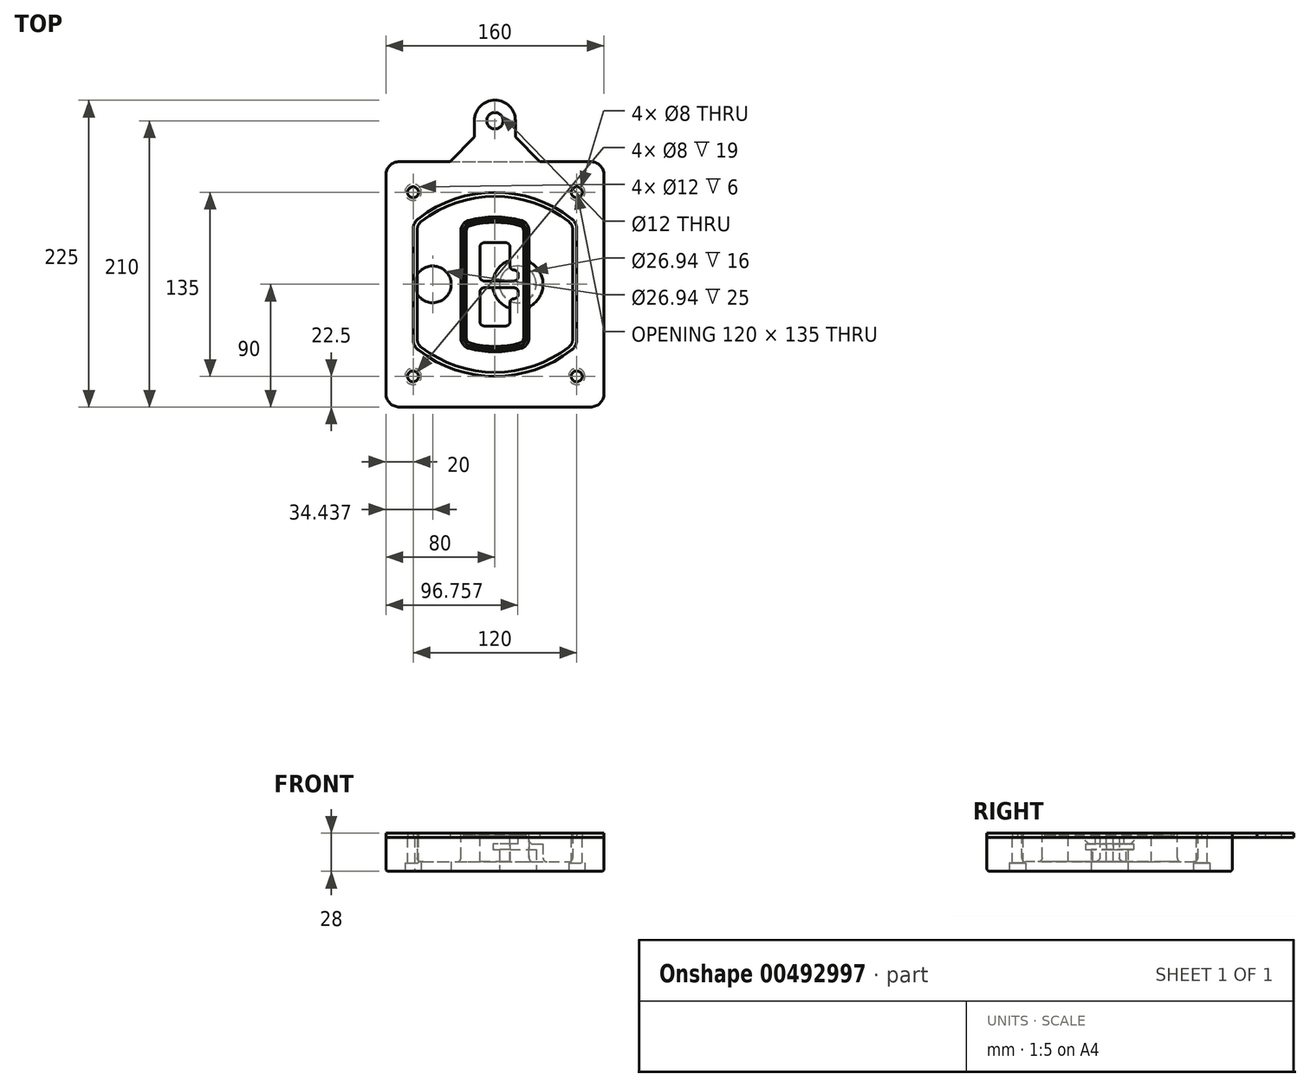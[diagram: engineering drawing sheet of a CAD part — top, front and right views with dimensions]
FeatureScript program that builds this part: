
annotation { "Feature Type Name" : "Feature", "Feature Type Description" : "" }
export const myFeature = defineFeature(function(context is Context, id is Id, definition is map)
    precondition{}
    {
        {
            var Q0;
            Q0=qCreatedBy(makeId("Top.planeOp"),FACE);
            var sketch = newSketch(context, id + "F0", { "sketchPlane" : qUnion([Q0])});
            skPoint(sketch, "E0.rect.middle", {"position": v(0, 0) * mm});
            skLineSegment(sketch, "E1.bottom", {"start": v(-70, -90) * mm, "end": v(70, -90) * mm});
            skLineSegment(sketch, "E1.top", {"start": v(-70, 90) * mm, "end": v(70, 90) * mm});
            skLineSegment(sketch, "E1.left", {"start": v(-80, -80) * mm, "end": v(-80, 80) * mm});
            skLineSegment(sketch, "E1.right", {"start": v(80, -80) * mm, "end": v(80, 80) * mm});
            skLineSegment(sketch, "E2", {"start": v(-80, 90) * mm, "end": v(80, -90) * mm, "construction": true});
            skLineSegment(sketch, "E3", {"start": v(80, 90) * mm, "end": v(-80, -90) * mm, "construction": true});
            skCircle(sketch, "E4", {"center": v(-60, 67.5) * mm, "radius": 4 * mm});
            skCircle(sketch, "E5", {"center": v(60, 67.5) * mm, "radius": 4 * mm});
            skCircle(sketch, "E6", {"center": v(60, -67.5) * mm, "radius": 4 * mm});
            skCircle(sketch, "E7", {"center": v(-60, -67.5) * mm, "radius": 4 * mm});
            skLineSegment(sketch, "E8", {"start": v(-60, 67.5) * mm, "end": v(60, 67.5) * mm, "construction": true});
            skLineSegment(sketch, "E9", {"start": v(60, 67.5) * mm, "end": v(60, -67.5) * mm, "construction": true});
            skLineSegment(sketch, "E10", {"start": v(60, -67.5) * mm, "end": v(-60, -67.5) * mm, "construction": true});
            skLineSegment(sketch, "E11", {"start": v(-60, -67.5) * mm, "end": v(-60, 67.5) * mm, "construction": true});
            skLineSegment(sketch, "E12", {"start": v(-60, 40.3) * mm, "end": v(-60, -40.3) * mm});
            skLineSegment(sketch, "E13", {"start": v(60, 40.3) * mm, "end": v(60, -40.3) * mm});
            skArc(sketch, "E14", {"start": v(56.15, 48.18) * mm, "mid": v(0, 67.5) * mm, "end": v(-56.15, 48.18) * mm});
            skArc(sketch, "E15", {"start": v(-56.15, -48.18) * mm, "mid": v(0, -67.5) * mm, "end": v(56.15, -48.18) * mm});
            skLineSegment(sketch, "E16", {"start": v(-60, 0) * mm, "end": v(60, 0) * mm, "construction": true});
            skPoint(sketch, "E17.visualSharp", {"position": v(-60, -45) * mm});
            skArc(sketch, "E17.filletArc", {"start": v(-60, -40.3) * mm, "mid": v(-58.99, -44.68) * mm, "end": v(-56.15, -48.18) * mm});
            skPoint(sketch, "E18.visualSharp", {"position": v(-60, 45) * mm});
            skArc(sketch, "E18.filletArc", {"start": v(-56.15, 48.18) * mm, "mid": v(-58.99, 44.68) * mm, "end": v(-60, 40.3) * mm});
            skPoint(sketch, "E19.visualSharp", {"position": v(60, 45) * mm});
            skArc(sketch, "E19.filletArc", {"start": v(60, 40.3) * mm, "mid": v(58.99, 44.68) * mm, "end": v(56.15, 48.18) * mm});
            skPoint(sketch, "E20.visualSharp", {"position": v(60, -45) * mm});
            skArc(sketch, "E20.filletArc", {"start": v(56.15, -48.18) * mm, "mid": v(58.99, -44.68) * mm, "end": v(60, -40.3) * mm});
            skPoint(sketch, "E21.visualSharp", {"position": v(-80, 90) * mm});
            skArc(sketch, "E21.filletArc", {"start": v(-70, 90) * mm, "mid": v(-77.07, 87.07) * mm, "end": v(-80, 80) * mm});
            skPoint(sketch, "E22.visualSharp", {"position": v(80, 90) * mm});
            skArc(sketch, "E22.filletArc", {"start": v(80, 80) * mm, "mid": v(77.07, 87.07) * mm, "end": v(70, 90) * mm});
            skPoint(sketch, "E23.visualSharp", {"position": v(80, -90) * mm});
            skArc(sketch, "E23.filletArc", {"start": v(70, -90) * mm, "mid": v(77.07, -87.07) * mm, "end": v(80, -80) * mm});
            skPoint(sketch, "E24.visualSharp", {"position": v(-80, -90) * mm});
            skArc(sketch, "E24.filletArc", {"start": v(-80, -80) * mm, "mid": v(-77.07, -87.07) * mm, "end": v(-70, -90) * mm});
            skArc(sketch, "E25.0", {"start": v(57, 40.3) * mm, "mid": v(56.3, 43.36) * mm, "end": v(54.3, 45.81) * mm});
            skLineSegment(sketch, "E25.1", {"start": v(57, 40.3) * mm, "end": v(57, -40.3) * mm});
            skArc(sketch, "E25.2", {"start": v(54.3, -45.81) * mm, "mid": v(56.3, -43.36) * mm, "end": v(57, -40.3) * mm});
            skArc(sketch, "E25.3", {"start": v(-54.3, -45.81) * mm, "mid": v(0, -64.5) * mm, "end": v(54.3, -45.81) * mm});
            skArc(sketch, "E25.4", {"start": v(-57, -40.3) * mm, "mid": v(-56.3, -43.36) * mm, "end": v(-54.3, -45.81) * mm});
            skArc(sketch, "E25.5", {"start": v(54.3, 45.81) * mm, "mid": v(0, 64.5) * mm, "end": v(-54.3, 45.81) * mm});
            skLineSegment(sketch, "E25.6", {"start": v(-57, 40.3) * mm, "end": v(-57, -40.3) * mm});
            skArc(sketch, "E25.7", {"start": v(-54.3, 45.81) * mm, "mid": v(-56.3, 43.36) * mm, "end": v(-57, 40.3) * mm});
            skArc(sketch, "E26.0", {"start": v(-58.62, 51.33) * mm, "mid": v(-62.58, 46.43) * mm, "end": v(-64, 40.3) * mm});
            skArc(sketch, "E26.1", {"start": v(58.62, 51.33) * mm, "mid": v(0, 71.5) * mm, "end": v(-58.62, 51.33) * mm});
            skArc(sketch, "E26.2", {"start": v(64, 40.3) * mm, "mid": v(62.58, 46.43) * mm, "end": v(58.62, 51.33) * mm});
            skLineSegment(sketch, "E26.3", {"start": v(64, 40.3) * mm, "end": v(64, -40.3) * mm});
            skArc(sketch, "E26.4", {"start": v(58.62, -51.33) * mm, "mid": v(62.58, -46.43) * mm, "end": v(64, -40.3) * mm});
            skLineSegment(sketch, "E26.5", {"start": v(-64, 40.3) * mm, "end": v(-64, -40.3) * mm});
            skArc(sketch, "E26.6", {"start": v(-58.62, -51.33) * mm, "mid": v(0, -71.5) * mm, "end": v(58.62, -51.33) * mm});
            skArc(sketch, "E26.7", {"start": v(-64, -40.3) * mm, "mid": v(-62.58, -46.43) * mm, "end": v(-58.62, -51.33) * mm});
            skSolve(sketch);
        }
        {
            var Q0;
            Q0=makeQuery(id+"F0.imprint","IMPRINT",FACE,{"disambiguationData":[TD([[makeQuery(id+"F0.imprint","IMPRINT",EDGE,{"derivedFrom":sQuery(id+"F0.wireOp",EDGE,"E1.bottom")}),1.0]])]});
            var Q1;
            Q1=makeQuery(id+"F0.imprint","IMPRINT",FACE,{"disambiguationData":[TD([[makeQuery(id+"F0.imprint","IMPRINT",EDGE,{"derivedFrom":sQuery(id+"F0.wireOp",EDGE,"E12")}),1.0]])]});
            var Q2;
            Q2=makeQuery(id+"F0.imprint","IMPRINT",FACE,{"disambiguationData":[TD([[makeQuery(id+"F0.imprint","IMPRINT",EDGE,{"derivedFrom":sQuery(id+"F0.wireOp",EDGE,"E25.0")}),1.0]])]});
            var Q3;
            Q3=makeQuery(id+"F0.imprint","IMPRINT",FACE,{"disambiguationData":[TD([[makeQuery(id+"F0.imprint","IMPRINT",EDGE,{"derivedFrom":sQuery(id+"F0.wireOp",EDGE,"E12")}),-1.0]])]});
            extrude(context, id + "F1", {"entities" : qUnion([Q0, Q1, Q2, Q3]), "oppositeDirection" : true, "depth" : 25 * mm});
        }
        {
            var Q0;
            Q0=makeQuery(id+"F0.imprint","IMPRINT",FACE,{"disambiguationData":[TD([[makeQuery(id+"F0.imprint","IMPRINT",EDGE,{"derivedFrom":sQuery(id+"F0.wireOp",EDGE,"E12")}),1.0]])]});
            extrude(context, id + "F2", {"entities" : qUnion([Q0]), "operationType" : NewBodyOperationType.ADD, "depth" : 3 * mm});
        }
        {
            var Q0;
            Q0=makeQuery(id+"F0.imprint","IMPRINT",FACE,{"disambiguationData":[TD([[makeQuery(id+"F0.imprint","IMPRINT",EDGE,{"derivedFrom":sQuery(id+"F0.wireOp",EDGE,"E25.0")}),1.0]])]});
            extrude(context, id + "F3", {"entities" : qUnion([Q0]), "operationType" : NewBodyOperationType.REMOVE, "oppositeDirection" : true, "depth" : 18 * mm});
        }
        {
            var Q0;
            Q0=makeQuery(id+"F2.opExtrude","CAP_FACE",FACE,{"disambiguationData":[OSD([sQuery(id+"F0.wireOp",EDGE,"E12"),sQuery(id+"F0.wireOp",EDGE,"E13"),sQuery(id+"F0.wireOp",EDGE,"E14"),sQuery(id+"F0.wireOp",EDGE,"E15"),sQuery(id+"F0.wireOp",EDGE,"E17.filletArc"),sQuery(id+"F0.wireOp",EDGE,"E18.filletArc"),sQuery(id+"F0.wireOp",EDGE,"E19.filletArc"),sQuery(id+"F0.wireOp",EDGE,"E20.filletArc"),sQuery(id+"F0.wireOp",EDGE,"E25.0"),sQuery(id+"F0.wireOp",EDGE,"E25.1"),sQuery(id+"F0.wireOp",EDGE,"E25.2"),sQuery(id+"F0.wireOp",EDGE,"E25.3"),sQuery(id+"F0.wireOp",EDGE,"E25.4"),sQuery(id+"F0.wireOp",EDGE,"E25.5"),sQuery(id+"F0.wireOp",EDGE,"E25.6"),sQuery(id+"F0.wireOp",EDGE,"E25.7")])],"isStart":false});
            var sketch = newSketch(context, id + "F4", { "sketchPlane" : qUnion([Q0])});
            skArc(sketch, "E27.0", {"start": v(-19.08, -46.97) * mm, "mid": v(0, -49.5) * mm, "end": v(19.08, -46.97) * mm});
            skArc(sketch, "E28.0", {"start": v(19.08, 46.97) * mm, "mid": v(0, 49.5) * mm, "end": v(-19.08, 46.97) * mm});
            skLineSegment(sketch, "E29", {"start": v(-25, 39.25) * mm, "end": v(-25, -39.25) * mm});
            skLineSegment(sketch, "E30", {"start": v(25, 39.25) * mm, "end": v(25, -39.25) * mm});
            skLineSegment(sketch, "E31", {"start": v(-25, 45.1) * mm, "end": v(25, 45.1) * mm, "construction": true});
            skLineSegment(sketch, "E32", {"start": v(-25, -45.1) * mm, "end": v(25, -45.1) * mm, "construction": true});
            skPoint(sketch, "E33.visualSharp", {"position": v(-25, 45.1) * mm});
            skArc(sketch, "E33.filletArc", {"start": v(-19.08, 46.97) * mm, "mid": v(-23.35, 44.11) * mm, "end": v(-25, 39.25) * mm});
            skPoint(sketch, "E34.visualSharp", {"position": v(25, 45.1) * mm});
            skArc(sketch, "E34.filletArc", {"start": v(25, 39.25) * mm, "mid": v(23.35, 44.11) * mm, "end": v(19.08, 46.97) * mm});
            skPoint(sketch, "E35.visualSharp", {"position": v(25, -45.1) * mm});
            skArc(sketch, "E35.filletArc", {"start": v(19.08, -46.97) * mm, "mid": v(23.35, -44.11) * mm, "end": v(25, -39.25) * mm});
            skPoint(sketch, "E36.visualSharp", {"position": v(-25, -45.1) * mm});
            skArc(sketch, "E36.filletArc", {"start": v(-25, -39.25) * mm, "mid": v(-23.35, -44.11) * mm, "end": v(-19.08, -46.97) * mm});
            skArc(sketch, "E37.0", {"start": v(54.3, 45.81) * mm, "mid": v(0, 64.5) * mm, "end": v(-54.3, 45.81) * mm});
            skArc(sketch, "E37.1", {"start": v(-54.3, 45.81) * mm, "mid": v(-56.3, 43.36) * mm, "end": v(-57, 40.3) * mm});
            skLineSegment(sketch, "E37.2", {"start": v(-57, 40.3) * mm, "end": v(-57, -40.3) * mm});
            skArc(sketch, "E37.3", {"start": v(-57, -40.3) * mm, "mid": v(-56.3, -43.36) * mm, "end": v(-54.3, -45.81) * mm});
            skArc(sketch, "E37.4", {"start": v(-54.3, -45.81) * mm, "mid": v(0, -64.5) * mm, "end": v(54.3, -45.81) * mm});
            skArc(sketch, "E37.5", {"start": v(54.3, -45.81) * mm, "mid": v(56.3, -43.36) * mm, "end": v(57, -40.3) * mm});
            skLineSegment(sketch, "E37.6", {"start": v(57, 40.3) * mm, "end": v(57, -40.3) * mm});
            skArc(sketch, "E37.7", {"start": v(57, 40.3) * mm, "mid": v(56.3, 43.36) * mm, "end": v(54.3, 45.81) * mm});
            skLineSegment(sketch, "E38.0", {"start": v(23, 39.25) * mm, "end": v(23, -39.25) * mm});
            skArc(sketch, "E38.1", {"start": v(18.56, -45.04) * mm, "mid": v(21.76, -42.9) * mm, "end": v(23, -39.25) * mm});
            skArc(sketch, "E38.2", {"start": v(-18.56, -45.04) * mm, "mid": v(0, -47.5) * mm, "end": v(18.56, -45.04) * mm});
            skArc(sketch, "E38.3", {"start": v(-23, -39.25) * mm, "mid": v(-21.76, -42.9) * mm, "end": v(-18.56, -45.04) * mm});
            skLineSegment(sketch, "E38.4", {"start": v(-23, 39.25) * mm, "end": v(-23, -39.25) * mm});
            skArc(sketch, "E38.5", {"start": v(23, 39.25) * mm, "mid": v(21.76, 42.9) * mm, "end": v(18.56, 45.04) * mm});
            skArc(sketch, "E38.6", {"start": v(-18.56, 45.04) * mm, "mid": v(-21.76, 42.9) * mm, "end": v(-23, 39.25) * mm});
            skArc(sketch, "E38.7", {"start": v(18.56, 45.04) * mm, "mid": v(0, 47.5) * mm, "end": v(-18.56, 45.04) * mm});
            skArc(sketch, "E39.0", {"start": v(21, 39.25) * mm, "mid": v(20.18, 41.68) * mm, "end": v(18.04, 43.1) * mm});
            skLineSegment(sketch, "E39.1", {"start": v(21, 39.25) * mm, "end": v(21, -39.25) * mm});
            skArc(sketch, "E39.2", {"start": v(18.04, -43.1) * mm, "mid": v(20.18, -41.68) * mm, "end": v(21, -39.25) * mm});
            skArc(sketch, "E39.3", {"start": v(-18.04, -43.1) * mm, "mid": v(0, -45.5) * mm, "end": v(18.04, -43.1) * mm});
            skArc(sketch, "E39.4", {"start": v(-21, -39.25) * mm, "mid": v(-20.18, -41.68) * mm, "end": v(-18.04, -43.1) * mm});
            skArc(sketch, "E39.5", {"start": v(18.04, 43.1) * mm, "mid": v(0, 45.5) * mm, "end": v(-18.04, 43.1) * mm});
            skLineSegment(sketch, "E39.6", {"start": v(-21, 39.25) * mm, "end": v(-21, -39.25) * mm});
            skArc(sketch, "E39.7", {"start": v(-18.04, 43.1) * mm, "mid": v(-20.18, 41.68) * mm, "end": v(-21, 39.25) * mm});
            skLineSegment(sketch, "E40", {"start": v(-25, 0) * mm, "end": v(25, 0) * mm, "construction": true});
            skLineSegment(sketch, "E41", {"start": v(-11, 5.5) * mm, "end": v(-11, 27.5) * mm});
            skLineSegment(sketch, "E42", {"start": v(-8, 30.5) * mm, "end": v(8, 30.5) * mm});
            skLineSegment(sketch, "E43", {"start": v(11, 27.5) * mm, "end": v(11, 13.5) * mm});
            skLineSegment(sketch, "E44", {"start": v(14, 10.5) * mm, "end": v(14, 10.5) * mm});
            skLineSegment(sketch, "E45", {"start": v(17, 7.5) * mm, "end": v(17, 5.5) * mm});
            skLineSegment(sketch, "E46", {"start": v(14, 2.5) * mm, "end": v(-8, 2.5) * mm});
            skPoint(sketch, "E47.visualSharp", {"position": v(-11, 30.5) * mm});
            skArc(sketch, "E47.filletArc", {"start": v(-8, 30.5) * mm, "mid": v(-10.12, 29.62) * mm, "end": v(-11, 27.5) * mm});
            skPoint(sketch, "E48.visualSharp", {"position": v(11, 30.5) * mm});
            skArc(sketch, "E48.filletArc", {"start": v(11, 27.5) * mm, "mid": v(10.12, 29.62) * mm, "end": v(8, 30.5) * mm});
            skPoint(sketch, "E49.visualSharp", {"position": v(11, 10.5) * mm});
            skArc(sketch, "E49.filletArc", {"start": v(11, 13.5) * mm, "mid": v(11.88, 11.38) * mm, "end": v(14, 10.5) * mm});
            skPoint(sketch, "E50.visualSharp", {"position": v(17, 10.5) * mm});
            skArc(sketch, "E50.filletArc", {"start": v(17, 7.5) * mm, "mid": v(16.12, 9.62) * mm, "end": v(14, 10.5) * mm});
            skPoint(sketch, "E51.visualSharp", {"position": v(17, 2.5) * mm});
            skArc(sketch, "E51.filletArc", {"start": v(14, 2.5) * mm, "mid": v(16.12, 3.38) * mm, "end": v(17, 5.5) * mm});
            skPoint(sketch, "E52.visualSharp", {"position": v(-11, 2.5) * mm});
            skArc(sketch, "E52.filletArc", {"start": v(-11, 5.5) * mm, "mid": v(-10.12, 3.38) * mm, "end": v(-8, 2.5) * mm});
            skLineSegment(sketch, "E53.0.MirrorCS", {"start": v(14, -2.5) * mm, "end": v(-8, -2.5) * mm});
            skArc(sketch, "E54.0.MirrorCS", {"start": v(-11, -5.5) * mm, "mid": v(-10.12, -3.38) * mm, "end": v(-8, -2.5) * mm});
            skLineSegment(sketch, "E55.0.MirrorCS", {"start": v(-11, -5.5) * mm, "end": v(-11, -27.5) * mm});
            skArc(sketch, "E56.0.MirrorCS", {"start": v(-8, -30.5) * mm, "mid": v(-10.12, -29.62) * mm, "end": v(-11, -27.5) * mm});
            skLineSegment(sketch, "E57.0.MirrorCS", {"start": v(-8, -30.5) * mm, "end": v(8, -30.5) * mm});
            skArc(sketch, "E58.0.MirrorCS", {"start": v(11, -27.5) * mm, "mid": v(10.12, -29.62) * mm, "end": v(8, -30.5) * mm});
            skLineSegment(sketch, "E59.0.MirrorCS", {"start": v(11, -27.5) * mm, "end": v(11, -13.5) * mm});
            skArc(sketch, "E60.0.MirrorCS", {"start": v(11, -13.5) * mm, "mid": v(11.88, -11.38) * mm, "end": v(14, -10.5) * mm});
            skArc(sketch, "E61.0.MirrorCS", {"start": v(17, -7.5) * mm, "mid": v(16.12, -9.62) * mm, "end": v(14, -10.5) * mm});
            skLineSegment(sketch, "E62.0.MirrorCS", {"start": v(17, -7.5) * mm, "end": v(17, -5.5) * mm});
            skArc(sketch, "E63.0.MirrorCS", {"start": v(14, -2.5) * mm, "mid": v(16.12, -3.38) * mm, "end": v(17, -5.5) * mm});
            skSolve(sketch);
        }
        {
            var Q0;
            Q0=makeQuery(id+"F4.imprint","IMPRINT",FACE,{"disambiguationData":[TD([[makeQuery(id+"F4.imprint","IMPRINT",EDGE,{"derivedFrom":sQuery(id+"F4.wireOp",EDGE,"E27.0")}),1.0]])]});
            var Q1;
            Q1=makeQuery(id+"F4.imprint","IMPRINT",FACE,{"disambiguationData":[TD([[makeQuery(id+"F4.imprint","IMPRINT",EDGE,{"derivedFrom":sQuery(id+"F4.wireOp",EDGE,"E38.0")}),-1.0]])]});
            var Q2;
            Q2=makeQuery(id+"F4.imprint","IMPRINT",FACE,{"disambiguationData":[TD([[makeQuery(id+"F4.imprint","IMPRINT",EDGE,{"derivedFrom":sQuery(id+"F4.wireOp",EDGE,"E39.0")}),1.0]])]});
            extrude(context, id + "F5", {"entities" : qUnion([Q0, Q1, Q2]), "operationType" : NewBodyOperationType.ADD, "endBound" : BoundingType.UP_TO_NEXT, "oppositeDirection" : true, "depth" : 25 * mm});
        }
        {
            var Q0;
            Q0=makeQuery(id+"F4.imprint","IMPRINT",FACE,{"disambiguationData":[TD([[makeQuery(id+"F4.imprint","IMPRINT",EDGE,{"derivedFrom":sQuery(id+"F4.wireOp",EDGE,"E38.0")}),-1.0]])]});
            extrude(context, id + "F6", {"entities" : qUnion([Q0]), "operationType" : NewBodyOperationType.REMOVE, "oppositeDirection" : true, "depth" : 2 * mm});
        }
        {
            var Q0;
            Q0=makeQuery(id+"F1.opExtrude","CAP_FACE",FACE,{"disambiguationData":[OSD([sQuery(id+"F0.wireOp",EDGE,"E1.bottom"),sQuery(id+"F0.wireOp",EDGE,"E1.top"),sQuery(id+"F0.wireOp",EDGE,"E1.left"),sQuery(id+"F0.wireOp",EDGE,"E1.right"),sQuery(id+"F0.wireOp",EDGE,"E4"),sQuery(id+"F0.wireOp",EDGE,"E5"),sQuery(id+"F0.wireOp",EDGE,"E6"),sQuery(id+"F0.wireOp",EDGE,"E7"),sQuery(id+"F0.wireOp",EDGE,"E21.filletArc"),sQuery(id+"F0.wireOp",EDGE,"E22.filletArc"),sQuery(id+"F0.wireOp",EDGE,"E23.filletArc"),sQuery(id+"F0.wireOp",EDGE,"E24.filletArc")])],"isStart":false});
            var sketch = newSketch(context, id + "F7", { "sketchPlane" : qUnion([Q0])});
            skCircle(sketch, "E64", {"center": v(16.76, 0) * mm, "radius": 13.47 * mm});
            skCircle(sketch, "E65", {"center": v(-45.56, 0) * mm, "radius": 13.47 * mm});
            skLineSegment(sketch, "E66", {"start": v(80, 0) * mm, "end": v(-80, 0) * mm});
            skCircle(sketch, "E67", {"center": v(16.76, 0) * mm, "radius": 18.47 * mm});
            skCircle(sketch, "E68", {"center": v(60, -67.5) * mm, "radius": 6 * mm});
            skCircle(sketch, "E69", {"center": v(-60, -67.5) * mm, "radius": 6 * mm});
            skCircle(sketch, "E70", {"center": v(-60, 67.5) * mm, "radius": 6 * mm});
            skCircle(sketch, "E71", {"center": v(60, 67.5) * mm, "radius": 6 * mm});
            skSolve(sketch);
        }
        {
            var Q0;
            {var subQ1=sQuery(id+"F7.wireOp",EDGE,"E66");var subQ4=sQuery(id+"F7.wireOp",EDGE,"E64");var subQ6=makeQuery(id+"F7.imprint","INTERSECT",VERTEX,{"disambiguationData":[OD(0.0)],"derivedFrom":[subQ4,subQ1]});Q0=makeQuery(id+"F7.imprint","IMPRINT",FACE,{"disambiguationData":[TD([[makeQuery(id+"F7.imprint","IMPRINT",EDGE,{"disambiguationData":[TD([[subQ6,-1.0]])],"derivedFrom":subQ4}),-1.0]])]});}
            var Q1;
            {var subQ0=sQuery(id+"F7.wireOp",EDGE,"E66");var subQ1=sQuery(id+"F7.wireOp",EDGE,"E64");var subQ3=makeQuery(id+"F7.imprint","INTERSECT",VERTEX,{"disambiguationData":[OD(0.0)],"derivedFrom":[subQ1,subQ0]});Q1=makeQuery(id+"F7.imprint","IMPRINT",FACE,{"disambiguationData":[TD([[makeQuery(id+"F7.imprint","IMPRINT",EDGE,{"disambiguationData":[TD([[subQ3,-1.0]])],"derivedFrom":subQ1}),1.0]])]});}
            var Q2;
            {var subQ0=sQuery(id+"F7.wireOp",EDGE,"E66");var subQ1=sQuery(id+"F7.wireOp",EDGE,"E64");var subQ3=makeQuery(id+"F7.imprint","INTERSECT",VERTEX,{"disambiguationData":[OD(0.0)],"derivedFrom":[subQ1,subQ0]});Q2=makeQuery(id+"F7.imprint","IMPRINT",FACE,{"disambiguationData":[TD([[makeQuery(id+"F7.imprint","IMPRINT",EDGE,{"disambiguationData":[TD([[subQ3,1.0]])],"derivedFrom":subQ1}),1.0]])]});}
            var Q3;
            {var subQ1=sQuery(id+"F7.wireOp",EDGE,"E66");var subQ4=sQuery(id+"F7.wireOp",EDGE,"E64");var subQ6=makeQuery(id+"F7.imprint","INTERSECT",VERTEX,{"disambiguationData":[OD(0.0)],"derivedFrom":[subQ4,subQ1]});Q3=makeQuery(id+"F7.imprint","IMPRINT",FACE,{"disambiguationData":[TD([[makeQuery(id+"F7.imprint","IMPRINT",EDGE,{"disambiguationData":[TD([[subQ6,1.0]])],"derivedFrom":subQ4}),-1.0]])]});}
            extrude(context, id + "F8", {"entities" : qUnion([Q0, Q1, Q2, Q3]), "operationType" : NewBodyOperationType.ADD, "oppositeDirection" : true, "depth" : 20 * mm});
        }
        {
            var Q0;
            {var subQ0=sQuery(id+"F7.wireOp",EDGE,"E66");var subQ1=sQuery(id+"F7.wireOp",EDGE,"E64");var subQ3=makeQuery(id+"F7.imprint","INTERSECT",VERTEX,{"disambiguationData":[OD(0.0)],"derivedFrom":[subQ1,subQ0]});Q0=makeQuery(id+"F7.imprint","IMPRINT",FACE,{"disambiguationData":[TD([[makeQuery(id+"F7.imprint","IMPRINT",EDGE,{"disambiguationData":[TD([[subQ3,-1.0]])],"derivedFrom":subQ1}),1.0]])]});}
            var Q1;
            {var subQ0=sQuery(id+"F7.wireOp",EDGE,"E66");var subQ1=sQuery(id+"F7.wireOp",EDGE,"E64");var subQ3=makeQuery(id+"F7.imprint","INTERSECT",VERTEX,{"disambiguationData":[OD(0.0)],"derivedFrom":[subQ1,subQ0]});Q1=makeQuery(id+"F7.imprint","IMPRINT",FACE,{"disambiguationData":[TD([[makeQuery(id+"F7.imprint","IMPRINT",EDGE,{"disambiguationData":[TD([[subQ3,1.0]])],"derivedFrom":subQ1}),1.0]])]});}
            extrude(context, id + "F9", {"entities" : qUnion([Q0, Q1]), "operationType" : NewBodyOperationType.REMOVE, "oppositeDirection" : true, "depth" : 16 * mm});
        }
        {
            var Q0;
            {var subQ0=sQuery(id+"F7.wireOp",EDGE,"E66");var subQ1=sQuery(id+"F7.wireOp",EDGE,"E65");var subQ3=makeQuery(id+"F7.imprint","INTERSECT",VERTEX,{"disambiguationData":[OD(0.0)],"derivedFrom":[subQ1,subQ0]});Q0=makeQuery(id+"F7.imprint","IMPRINT",FACE,{"disambiguationData":[TD([[makeQuery(id+"F7.imprint","IMPRINT",EDGE,{"disambiguationData":[TD([[subQ3,-1.0]])],"derivedFrom":subQ1}),1.0]])]});}
            var Q1;
            {var subQ0=sQuery(id+"F7.wireOp",EDGE,"E66");var subQ1=sQuery(id+"F7.wireOp",EDGE,"E65");var subQ3=makeQuery(id+"F7.imprint","INTERSECT",VERTEX,{"disambiguationData":[OD(0.0)],"derivedFrom":[subQ1,subQ0]});Q1=makeQuery(id+"F7.imprint","IMPRINT",FACE,{"disambiguationData":[TD([[makeQuery(id+"F7.imprint","IMPRINT",EDGE,{"disambiguationData":[TD([[subQ3,1.0]])],"derivedFrom":subQ1}),1.0]])]});}
            extrude(context, id + "F10", {"entities" : qUnion([Q0, Q1]), "operationType" : NewBodyOperationType.REMOVE, "oppositeDirection" : true, "depth" : 25 * mm});
        }
        {
            var Q0;
            Q0=makeQuery(id+"F7.imprint","IMPRINT",FACE,{"disambiguationData":[TD([[makeQuery(id+"F7.imprint","IMPRINT",EDGE,{"derivedFrom":sQuery(id+"F7.wireOp",EDGE,"E68")}),1.0]])]});
            var Q1;
            Q1=makeQuery(id+"F7.imprint","IMPRINT",FACE,{"disambiguationData":[TD([[makeQuery(id+"F7.imprint","IMPRINT",EDGE,{"derivedFrom":makeQuery(id+"F1.opExtrude","CAP_EDGE",EDGE,{"disambiguationData":[OSD([sQuery(id+"F0.wireOp",EDGE,"E5")])],"isStart":false})}),-1.0]])]});
            var Q2;
            Q2=makeQuery(id+"F7.imprint","IMPRINT",FACE,{"disambiguationData":[TD([[makeQuery(id+"F7.imprint","IMPRINT",EDGE,{"derivedFrom":sQuery(id+"F7.wireOp",EDGE,"E69")}),1.0]])]});
            var Q3;
            Q3=makeQuery(id+"F7.imprint","IMPRINT",FACE,{"disambiguationData":[TD([[makeQuery(id+"F7.imprint","IMPRINT",EDGE,{"derivedFrom":makeQuery(id+"F1.opExtrude","CAP_EDGE",EDGE,{"disambiguationData":[OSD([sQuery(id+"F0.wireOp",EDGE,"E4")])],"isStart":false})}),-1.0]])]});
            var Q4;
            Q4=makeQuery(id+"F7.imprint","IMPRINT",FACE,{"disambiguationData":[TD([[makeQuery(id+"F7.imprint","IMPRINT",EDGE,{"derivedFrom":sQuery(id+"F7.wireOp",EDGE,"E70")}),1.0]])]});
            var Q5;
            Q5=makeQuery(id+"F7.imprint","IMPRINT",FACE,{"disambiguationData":[TD([[makeQuery(id+"F7.imprint","IMPRINT",EDGE,{"derivedFrom":makeQuery(id+"F1.opExtrude","CAP_EDGE",EDGE,{"disambiguationData":[OSD([sQuery(id+"F0.wireOp",EDGE,"E7")])],"isStart":false})}),-1.0]])]});
            var Q6;
            Q6=makeQuery(id+"F7.imprint","IMPRINT",FACE,{"disambiguationData":[TD([[makeQuery(id+"F7.imprint","IMPRINT",EDGE,{"derivedFrom":sQuery(id+"F7.wireOp",EDGE,"E71")}),1.0]])]});
            var Q7;
            Q7=makeQuery(id+"F7.imprint","IMPRINT",FACE,{"disambiguationData":[TD([[makeQuery(id+"F7.imprint","IMPRINT",EDGE,{"derivedFrom":makeQuery(id+"F1.opExtrude","CAP_EDGE",EDGE,{"disambiguationData":[OSD([sQuery(id+"F0.wireOp",EDGE,"E6")])],"isStart":false})}),-1.0]])]});
            extrude(context, id + "F11", {"entities" : qUnion([Q0, Q1, Q2, Q3, Q4, Q5, Q6, Q7]), "operationType" : NewBodyOperationType.REMOVE, "oppositeDirection" : true, "depth" : 6 * mm});
        }
        {
            var Q0;
            Q0=makeQuery(id+"F9.boolean.opBoolean","COPY",FACE,{"derivedFrom":makeQuery(id+"F9.opExtrude","CAP_FACE",FACE,{"disambiguationData":[OSD([sQuery(id+"F7.wireOp",EDGE,"E64")])],"isStart":false})});
            var sketch = newSketch(context, id + "F12", { "sketchPlane" : qUnion([Q0])});
            skArc(sketch, "E72.0", {"start": v(11, 17.55) * mm, "mid": v(2.57, 11.82) * mm, "end": v(-1.54, 2.5) * mm});
            skArc(sketch, "E72.1", {"start": v(-1.54, -2.5) * mm, "mid": v(2.57, -11.82) * mm, "end": v(11, -17.55) * mm});
            skLineSegment(sketch, "E73", {"start": v(-1.54, -2.5) * mm, "end": v(14, -2.5) * mm});
            skLineSegment(sketch, "E74.0", {"start": v(14, 2.5) * mm, "end": v(-1.54, 2.5) * mm});
            skArc(sketch, "E74.1", {"start": v(14, 2.5) * mm, "mid": v(16.12, 3.38) * mm, "end": v(17, 5.5) * mm});
            skLineSegment(sketch, "E74.2", {"start": v(17, 7.5) * mm, "end": v(17, 5.5) * mm});
            skArc(sketch, "E74.3", {"start": v(17, 7.5) * mm, "mid": v(16.12, 9.62) * mm, "end": v(14, 10.5) * mm});
            skArc(sketch, "E74.4", {"start": v(11, 13.5) * mm, "mid": v(11.88, 11.38) * mm, "end": v(14, 10.5) * mm});
            skLineSegment(sketch, "E74.5", {"start": v(11, 17.55) * mm, "end": v(11, 13.5) * mm});
            skLineSegment(sketch, "E74.7", {"start": v(14, -2.5) * mm, "end": v(-1.54, -2.5) * mm});
            skArc(sketch, "E74.8", {"start": v(14, -2.5) * mm, "mid": v(16.12, -3.38) * mm, "end": v(17, -5.5) * mm});
            skLineSegment(sketch, "E74.9", {"start": v(17, -7.5) * mm, "end": v(17, -5.5) * mm});
            skArc(sketch, "E74.10", {"start": v(17, -7.5) * mm, "mid": v(16.12, -9.62) * mm, "end": v(14, -10.5) * mm});
            skArc(sketch, "E74.11", {"start": v(11, -13.5) * mm, "mid": v(11.88, -11.38) * mm, "end": v(14, -10.5) * mm});
            skLineSegment(sketch, "E74.12", {"start": v(11, -17.55) * mm, "end": v(11, -13.5) * mm});
            skPoint(sketch, "E75.orphan", {"position": v(11, -27.5) * mm});
            skPoint(sketch, "E76.orphan", {"position": v(-8, -2.5) * mm});
            skPoint(sketch, "E77.orphan", {"position": v(-8, 2.5) * mm});
            skPoint(sketch, "E78.orphan", {"position": v(11, 27.5) * mm});
            skSolve(sketch);
        }
        {
            var Q0;
            {var subQ7=sQuery(id+"F12.wireOp",EDGE,"E72.0");var subQ14=sQuery(id+"F12.wireOp",EDGE,"E72.1");var subQ16=sQuery(id+"F12.wireOp",EDGE,"E74.1");var subQ18=sQuery(id+"F12.wireOp",EDGE,"E74.8");Q0=qUnion([makeQuery(id+"F12.imprint","IMPRINT",FACE,{"disambiguationData":[TD([[makeQuery(id+"F12.imprint","IMPRINT",EDGE,{"derivedFrom":subQ7}),1.0]])]}),makeQuery(id+"F12.imprint","IMPRINT",FACE,{"disambiguationData":[TD([[makeQuery(id+"F12.imprint","IMPRINT",EDGE,{"derivedFrom":subQ14}),1.0]])]}),makeQuery(id+"F12.imprint","IMPRINT",FACE,{"disambiguationData":[TD([[makeQuery(id+"F12.imprint","IMPRINT",EDGE,{"derivedFrom":subQ16}),1.0]])]}),makeQuery(id+"F12.imprint","IMPRINT",FACE,{"disambiguationData":[TD([[makeQuery(id+"F12.imprint","IMPRINT",EDGE,{"derivedFrom":subQ18}),-1.0]])]})]);}
            var Q1;
            Q1=makeQuery(id+"F5.boolean.opBoolean","SPLIT",FACE,{"disambiguationData":[TD([makeQuery(id+"F5.opExtrude","SWEPT_FACE",FACE,{"disambiguationData":[OSD([sQuery(id+"F4.wireOp",EDGE,"E41")])]})])],"derivedFrom":makeQuery(id+"F3.boolean.opBoolean","COPY",FACE,{"derivedFrom":makeQuery(id+"F3.opExtrude","CAP_FACE",FACE,{"disambiguationData":[OSD([sQuery(id+"F0.wireOp",EDGE,"E25.0"),sQuery(id+"F0.wireOp",EDGE,"E25.1"),sQuery(id+"F0.wireOp",EDGE,"E25.2"),sQuery(id+"F0.wireOp",EDGE,"E25.3"),sQuery(id+"F0.wireOp",EDGE,"E25.4"),sQuery(id+"F0.wireOp",EDGE,"E25.5"),sQuery(id+"F0.wireOp",EDGE,"E25.6"),sQuery(id+"F0.wireOp",EDGE,"E25.7")])],"isStart":false})})});
            extrude(context, id + "F13", {"entities" : qUnion([Q0]), "operationType" : NewBodyOperationType.REMOVE, "endBound" : BoundingType.UP_TO_SURFACE, "endBoundEntityFace" : qUnion([Q1]), "depth" : 25 * mm});
        }
        {
            var Q0;
            Q0=makeQuery(id+"F3.boolean.opBoolean","COPY",EDGE,{"derivedFrom":makeQuery(id+"F3.opExtrude","CAP_EDGE",EDGE,{"disambiguationData":[OSD([sQuery(id+"F0.wireOp",EDGE,"E25.6")])],"isStart":false})});
            var Q1;
            Q1=makeQuery(id+"F8.boolean.opBoolean","INTERSECT",EDGE,{"derivedFrom":[makeQuery(id+"F5.opExtrude","SWEPT_FACE",FACE,{"disambiguationData":[OSD([sQuery(id+"F4.wireOp",EDGE,"E30")])]}),makeQuery(id+"F8.opExtrude","CAP_FACE",FACE,{"disambiguationData":[OSD([sQuery(id+"F7.wireOp",EDGE,"E67")])],"isStart":false})]});
            var Q2;
            Q2=makeQuery(id+"F8.boolean.opBoolean","INTERSECT",EDGE,{"disambiguationData":[OD(1.0)],"derivedFrom":[makeQuery(id+"F5.opExtrude","SWEPT_FACE",FACE,{"disambiguationData":[OSD([sQuery(id+"F4.wireOp",EDGE,"E30")])]}),makeQuery(id+"F8.opExtrude","SWEPT_FACE",FACE,{"disambiguationData":[OSD([sQuery(id+"F7.wireOp",EDGE,"E67")])]})]});
            var Q3;
            {var subQ0=sQuery(id+"F4.wireOp",EDGE,"E30");Q3=makeQuery(id+"F8.boolean.opBoolean","SPLIT",EDGE,{"disambiguationData":[TD([makeQuery(id+"F5.opExtrude","SWEPT_FACE",FACE,{"disambiguationData":[OSD([sQuery(id+"F4.wireOp",EDGE,"E35.filletArc")])]})])],"derivedFrom":makeQuery(id+"F5.opExtrude","CAP_EDGE",EDGE,{"disambiguationData":[OSD([subQ0])],"isStart":false})});}
            var Q4;
            {var subQ0=sQuery(id+"F0.wireOp",EDGE,"E25.7");var subQ1=sQuery(id+"F0.wireOp",EDGE,"E25.1");var subQ2=sQuery(id+"F0.wireOp",EDGE,"E25.6");var subQ3=sQuery(id+"F0.wireOp",EDGE,"E25.5");var subQ4=sQuery(id+"F0.wireOp",EDGE,"E25.4");var subQ5=sQuery(id+"F0.wireOp",EDGE,"E25.0");var subQ6=sQuery(id+"F0.wireOp",EDGE,"E25.2");var subQ7=sQuery(id+"F0.wireOp",EDGE,"E25.3");Q4=makeQuery(id+"F8.boolean.opBoolean","INTERSECT",EDGE,{"derivedFrom":[makeQuery(id+"F5.boolean.opBoolean","SPLIT",FACE,{"disambiguationData":[TD([makeQuery(id+"F2.opExtrude","SWEPT_FACE",FACE,{"disambiguationData":[OSD([subQ5])]})])],"derivedFrom":makeQuery(id+"F3.boolean.opBoolean","COPY",FACE,{"derivedFrom":makeQuery(id+"F3.opExtrude","CAP_FACE",FACE,{"disambiguationData":[OSD([subQ5,subQ1,subQ6,subQ7,subQ4,subQ3,subQ2,subQ0])],"isStart":false})})}),makeQuery(id+"F8.opExtrude","SWEPT_FACE",FACE,{"disambiguationData":[OSD([sQuery(id+"F7.wireOp",EDGE,"E67")])]})]});}
            var Q5;
            Q5=makeQuery(id+"F8.boolean.opBoolean","INTERSECT",EDGE,{"disambiguationData":[OD(0.0)],"derivedFrom":[makeQuery(id+"F5.opExtrude","SWEPT_FACE",FACE,{"disambiguationData":[OSD([sQuery(id+"F4.wireOp",EDGE,"E30")])]}),makeQuery(id+"F8.opExtrude","SWEPT_FACE",FACE,{"disambiguationData":[OSD([sQuery(id+"F7.wireOp",EDGE,"E67")])]})]});
            fillet(context, id + "F14", {"entities" : qUnion([Q0, Q1, Q2, Q3, Q4, Q5]), "radius" : 3 * mm, "tangentPropagation" : true, "allowEdgeOverflow" : false});
        }
        {
            var Q0;
            Q0=makeQuery(id+"F1.opExtrude","CAP_EDGE",EDGE,{"disambiguationData":[OSD([sQuery(id+"F0.wireOp",EDGE,"E1.bottom")])],"isStart":false});
            fillet(context, id + "F15", {"entities" : qUnion([Q0]), "radius" : 2 * mm, "tangentPropagation" : true, "allowEdgeOverflow" : false});
        }
        {
            var Q0;
            {var subQ0=sQuery(id+"F0.wireOp",EDGE,"E21.filletArc");var subQ1=sQuery(id+"F0.wireOp",EDGE,"E7");var subQ2=sQuery(id+"F0.wireOp",EDGE,"E6");var subQ3=sQuery(id+"F0.wireOp",EDGE,"E5");var subQ4=sQuery(id+"F0.wireOp",EDGE,"E4");var subQ5=sQuery(id+"F0.wireOp",EDGE,"E22.filletArc");var subQ6=sQuery(id+"F0.wireOp",EDGE,"E1.bottom");var subQ7=sQuery(id+"F0.wireOp",EDGE,"E1.right");var subQ8=sQuery(id+"F0.wireOp",EDGE,"E1.top");var subQ9=sQuery(id+"F0.wireOp",EDGE,"E1.left");var subQ10=sQuery(id+"F0.wireOp",EDGE,"E23.filletArc");var subQ11=sQuery(id+"F0.wireOp",EDGE,"E24.filletArc");Q0=makeQuery(id+"F2.boolean.opBoolean","SPLIT",FACE,{"disambiguationData":[TD([makeQuery(id+"F1.opExtrude","SWEPT_FACE",FACE,{"disambiguationData":[OSD([subQ6])]})])],"derivedFrom":makeQuery(id+"F1.opExtrude","CAP_FACE",FACE,{"disambiguationData":[OSD([subQ6,subQ8,subQ9,subQ7,subQ4,subQ3,subQ2,subQ1,subQ0,subQ5,subQ10,subQ11])],"isStart":true})});}
            var sketch = newSketch(context, id + "F16", { "sketchPlane" : qUnion([Q0])});
            skLineSegment(sketch, "E79", {"start": v(0, 90) * mm, "end": v(0, 120) * mm, "construction": true});
            skLineSegment(sketch, "E80", {"start": v(-33, 90) * mm, "end": v(-15, 108) * mm});
            skLineSegment(sketch, "E81", {"start": v(33, 90) * mm, "end": v(15, 108) * mm});
            skLineSegment(sketch, "E82", {"start": v(-15, 108) * mm, "end": v(-15, 120) * mm});
            skLineSegment(sketch, "E83", {"start": v(15, 108) * mm, "end": v(15, 120) * mm});
            skCircle(sketch, "E84", {"center": v(0, 120) * mm, "radius": 6 * mm});
            skArc(sketch, "E85", {"start": v(15, 120) * mm, "mid": v(0, 135) * mm, "end": v(-15, 120) * mm});
            skLineSegment(sketch, "E86", {"start": v(-80, 0) * mm, "end": v(80, 0) * mm, "construction": true});
            skArc(sketch, "E87.MirrorCS", {"start": v(15, -120) * mm, "mid": v(0, -135) * mm, "end": v(-15, -120) * mm});
            skCircle(sketch, "E88.MirrorC", {"center": v(0, -120) * mm, "radius": 6 * mm});
            skLineSegment(sketch, "E89.MirrorCS", {"start": v(15, -108) * mm, "end": v(15, -120) * mm});
            skLineSegment(sketch, "E90.MirrorCS", {"start": v(-15, -108) * mm, "end": v(-15, -120) * mm});
            skLineSegment(sketch, "E91.MirrorCS", {"start": v(33, -90) * mm, "end": v(15, -108) * mm});
            skLineSegment(sketch, "E92.MirrorCS", {"start": v(-33, -90) * mm, "end": v(-15, -108) * mm});
            skLineSegment(sketch, "E93.MirrorCS", {"start": v(0, -90) * mm, "end": v(0, -120) * mm, "construction": true});
            skSolve(sketch);
        }
        {
            var Q0;
            {var subQ0=sQuery(id+"F16.wireOp",EDGE,"E80");Q0=makeQuery(id+"F16.imprint","IMPRINT",FACE,{"disambiguationData":[TD([[makeQuery(id+"F16.imprint","IMPRINT",EDGE,{"derivedFrom":subQ0}),-1.0]])]});}
            var Q1;
            Q1=makeQuery(id+"F16.imprint","IMPRINT",FACE,{"disambiguationData":[TD([[makeQuery(id+"F16.imprint","IMPRINT",EDGE,{"derivedFrom":makeQuery(id+"F1.opExtrude","CAP_EDGE",EDGE,{"disambiguationData":[OSD([sQuery(id+"F0.wireOp",EDGE,"E1.left")])],"isStart":true})}),-1.0]])]});
            var Q2;
            Q2=makeQuery(id+"F16.imprint","IMPRINT",FACE,{"disambiguationData":[TD([[makeQuery(id+"F16.imprint","IMPRINT",EDGE,{"derivedFrom":sQuery(id+"F16.wireOp",EDGE,"E87.MirrorCS")}),-1.0]])]});
            var Q3;
            Q3=makeQuery(id+"F2.opExtrude","CAP_FACE",FACE,{"disambiguationData":[OSD([sQuery(id+"F0.wireOp",EDGE,"E12"),sQuery(id+"F0.wireOp",EDGE,"E13"),sQuery(id+"F0.wireOp",EDGE,"E14"),sQuery(id+"F0.wireOp",EDGE,"E15"),sQuery(id+"F0.wireOp",EDGE,"E17.filletArc"),sQuery(id+"F0.wireOp",EDGE,"E18.filletArc"),sQuery(id+"F0.wireOp",EDGE,"E19.filletArc"),sQuery(id+"F0.wireOp",EDGE,"E20.filletArc"),sQuery(id+"F0.wireOp",EDGE,"E25.0"),sQuery(id+"F0.wireOp",EDGE,"E25.1"),sQuery(id+"F0.wireOp",EDGE,"E25.2"),sQuery(id+"F0.wireOp",EDGE,"E25.3"),sQuery(id+"F0.wireOp",EDGE,"E25.4"),sQuery(id+"F0.wireOp",EDGE,"E25.5"),sQuery(id+"F0.wireOp",EDGE,"E25.6"),sQuery(id+"F0.wireOp",EDGE,"E25.7")])],"isStart":false});
            extrude(context, id + "F17", {"entities" : qUnion([Q0, Q1, Q2]), "endBound" : BoundingType.UP_TO_SURFACE, "endBoundEntityFace" : qUnion([Q3]), "depth" : 25 * mm});
        }
    });
